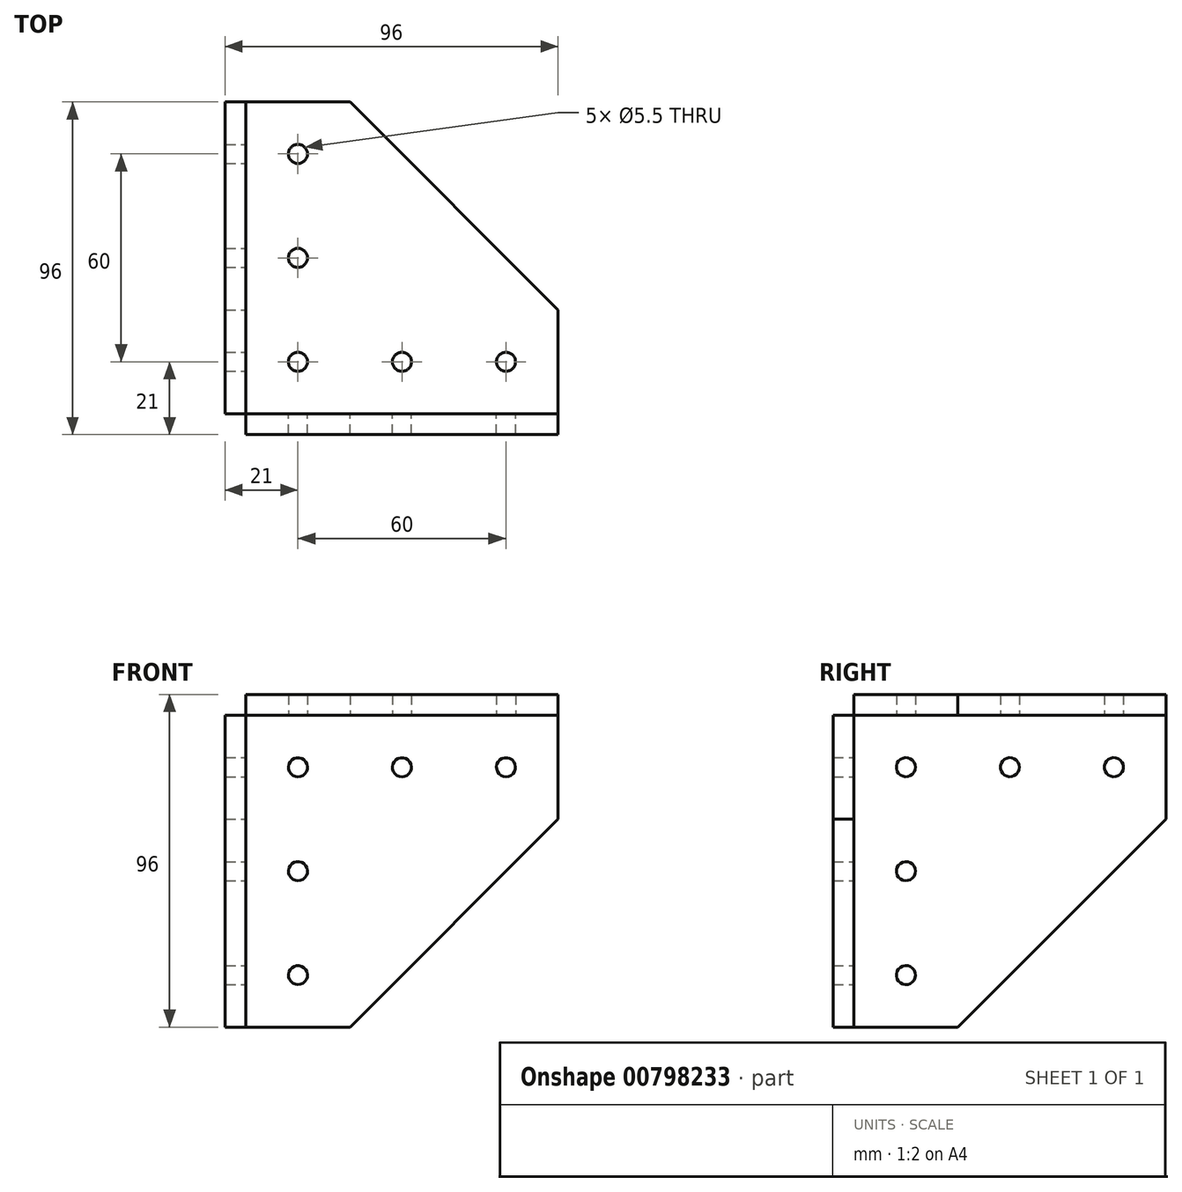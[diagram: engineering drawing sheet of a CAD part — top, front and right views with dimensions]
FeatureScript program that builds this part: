
annotation { "Feature Type Name" : "Feature", "Feature Type Description" : "" }
export const myFeature = defineFeature(function(context is Context, id is Id, definition is map)
    precondition{}
    {
        {
            var Q0;
            Q0=qCreatedBy(makeId("Top.planeOp"),FACE);
            var sketch = newSketch(context, id + "F0", { "sketchPlane" : qUnion([Q0])});
            skLineSegment(sketch, "E0", {"start": v(15, 75) * mm, "end": v(-15, 75) * mm});
            skLineSegment(sketch, "E1", {"start": v(-15, 75) * mm, "end": v(-15, -15) * mm});
            skLineSegment(sketch, "E2", {"start": v(-15, -15) * mm, "end": v(75, -15) * mm});
            skLineSegment(sketch, "E3", {"start": v(75, -15) * mm, "end": v(75, 15) * mm});
            skLineSegment(sketch, "E4", {"start": v(75, 15) * mm, "end": v(15, 75) * mm});
            skLineSegment(sketch, "E5", {"start": v(0, 75) * mm, "end": v(0, -15) * mm, "construction": true});
            skLineSegment(sketch, "E6", {"start": v(75, 0) * mm, "end": v(-15, 0) * mm, "construction": true});
            skCircle(sketch, "E7", {"center": v(0, 0) * mm, "radius": 2.75 * mm});
            skCircle(sketch, "E8.0.1.0", {"center": v(0, 30) * mm, "radius": 2.75 * mm});
            skCircle(sketch, "E8.0.2.0", {"center": v(0, 60) * mm, "radius": 2.75 * mm});
            skCircle(sketch, "E8.1.0.0", {"center": v(30, 0) * mm, "radius": 2.75 * mm});
            skCircle(sketch, "E8.1.1.0", {"center": v(30, 30) * mm, "radius": 2.75 * mm, "construction": true});
            skCircle(sketch, "E8.1.2.0", {"center": v(30, 60) * mm, "radius": 2.75 * mm, "construction": true});
            skCircle(sketch, "E8.2.0.0", {"center": v(60, 0) * mm, "radius": 2.75 * mm});
            skCircle(sketch, "E8.2.1.0", {"center": v(60, 30) * mm, "radius": 2.75 * mm, "construction": true});
            skCircle(sketch, "E8.2.2.0", {"center": v(60, 60) * mm, "radius": 2.75 * mm, "construction": true});
            skLineSegment(sketch, "E8.direction1", {"start": v(0, 0) * mm, "end": v(30, 0) * mm, "construction": true});
            skLineSegment(sketch, "E8.direction2", {"start": v(0, 0) * mm, "end": v(0, 30) * mm, "construction": true});
            skSolve(sketch);
        }
        {
            var Q0;
            Q0=makeQuery(id+"F0.imprint","IMPRINT",FACE,{"disambiguationData":[TD([[makeQuery(id+"F0.imprint","IMPRINT",EDGE,{"derivedFrom":sQuery(id+"F0.wireOp",EDGE,"E0")}),1.0]])]});
            extrude(context, id + "F1", {"entities" : qUnion([Q0]), "depth" : 6 * mm, "offsetDistance" : 25 * mm});
        }
        {
            var Q0;
            Q0=qCreatedBy(makeId("Front.planeOp"),FACE);
            var Q1;
            Q1=qCreatedBy(makeId("Right.planeOp"),FACE);
            cPlane(context, id + "F2", {"entities" : qUnion([Q0, Q1]), "cplaneType" : CPlaneType.MID_PLANE, "offset" : 25 * mm, "flipAlignment" : true, "width" : 150 * mm, "height" : 150 * mm});
        }
        {
            var Q0;
            Q0=qCreatedBy(id+"F2.planeOp",FACE);
            var sketch = newSketch(context, id + "F3", { "sketchPlane" : qUnion([Q0])});
            skLineSegment(sketch, "E9", {"start": v(-21.21, 0) * mm, "end": v(-43.02, 15.42) * mm});
            skSolve(sketch);
        }
        {
            var Q0;
            Q0=makeQuery(id+"F1.opExtrude","SWEPT_BODY",BODY,{"disambiguationData":[OSD([sQuery(id+"F0.wireOp",EDGE,"E0"),sQuery(id+"F0.wireOp",EDGE,"E1"),sQuery(id+"F0.wireOp",EDGE,"E2"),sQuery(id+"F0.wireOp",EDGE,"E3"),sQuery(id+"F0.wireOp",EDGE,"E4"),sQuery(id+"F0.wireOp",EDGE,"E7"),sQuery(id+"F0.wireOp",EDGE,"E8.0.1.0"),sQuery(id+"F0.wireOp",EDGE,"E8.0.2.0"),sQuery(id+"F0.wireOp",EDGE,"E8.1.0.0"),sQuery(id+"F0.wireOp",EDGE,"E8.2.0.0")])]});
            var Q1;
            Q1=sQuery(id+"F3.wireOp",EDGE,"E9");
            circularPattern(context, id + "F4", {"entities" : qUnion([Q0]), "axis" : qUnion([Q1]), "angle" : 360 * degree, "instanceCount" : 3, "equalSpace" : true});
        }
    });
